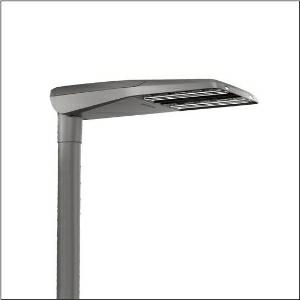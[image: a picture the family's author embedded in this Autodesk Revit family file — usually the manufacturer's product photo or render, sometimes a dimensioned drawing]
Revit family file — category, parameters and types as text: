
# Revit family: streetlight_sl_11_iq_midi___st1_2a_5xc3a51e08le_ac55
name_source: partatom
category: Lighting Fixtures
units: mm (PartAtom-declared; Revit-internal decimal feet)

## family parameters
Cut with Voids When Loaded = No
Host = Face
Light Source = No
Part Type = Normal
Room Calculation Point = No
Round Connector Dimension = Use Diameter
Shared = No

## types (1)
- --- (1 x LED, 9210 lm, 60.4 W, 3000K)
    Apparent Load = 60 VA
    CIE Flux Codes = 32 70 96 100 100
    Color Rendering = 70
    Color Temperature = 3000K
    Default Elevation = 1800 mm
    Description = Streetlight SL 11 iQ midi, mast luminaire, primary light control with 3 zone facetted reflector, of plastic, silver coated, highly specular, primary optical cover: cover, of PMMA, transparent, light distribution: ST1.2a, light emission: direct distribution, primary light characteristic: asymmetric, installation type: post-top, side-entry, lamps: LED, High Power LED, rated values: 9.210lm | 60,4W | 152,5lm/W (begin service life); end service life: 9.210lm | 62,5W; at 50% lumin. flux: 4.605lm | 29,6W | 155,6lm/W, colour temperature: 3000K, colour rendering: CRI > 70, light colour: 730, light setting 1 begin service life: 100% | 9.210lm | 60,4W | 152,5lm/W | 3.000K, light setting 1 end service life: 62,5W, further light settings possible, control: optimised constant luminous flux control (CLO 2.0), Desk-Remote (wireless, voltage-free reading and setting of iQ features in the workshop via application-optimized NFC function/RFID function), Light-Fading, Smart-Wire, Night-Set, Lumen-Switch, Temp-Guard, Auto-Match, with cable H07RN-F 5x 1.5mm², mains connection: 230..240V, AC, 50/60Hz, connection cable pre-assembled, cable length: 8,5m, luminaire housing, of diecast aluminium, powder-coated, Siteco® metallic grey (DB 702S), please order mast flange separately, inclination adjustable without tools: 0°, 5°, 10°, 15° (post-top) | 0°, -5°, -10°, -15° (side-entry), sealing non-destructively replaceable, multi-level sealing system, length: 780mm, width: 376mm, height: 118mm, mast flange for spigot size: 42mm (side-entry): 5XC10008XM4, 60/48mm (side-entry/post-top): 5XC10108XM2, 76/60mm (side-entry/post-top): 5XC10108XM1, equipment: standard, protection rating (complete): IP66, insulation class (complete): insulation class II (safety insulation), certification: CE, ENEC, ENEC+, VDE, impact resistance: IK10, permissible operating ambient temperature for outdoor applications: -25..+50°C, standard-compliant lighting for roads and squares, Environmental Product Declaration (EPD) tested and certified by an independent institute, packaging unit: 1 piece

Light Distribution: ST1.2a
    Height = 118 mm
    Lamp = 1 x LED
    Lamp Light Flux = 9210 lm
    Lamp Power = 60.4 W
    Lamp count = 1
    Length = 780 mm
    Luminous efficacy = 152 lm/W
    Manufacturer = Siteco
    ModVariant = No
    Model = 5XC3A51E08LE
    Number of Poles = 1
    OnlyDefault = Yes
    Power Factor = 1
    Product Name = Streetlight SL 11 iQ midi | ST1.2a
    Product group = mast luminaire | pylon top
    ProductGroupID = 6100
    Protection Class = Protection class II
    Protection Degree = IP 66
    RLX_Detail_Level = 1
    RLX_Emergency_Light_Flux = 0 lm
    RLX_Emergency_Type = 0
    RLX_Emergency_Type_DB = No
    RlxData = <blob elided: 70713 chars, md5=c5067b52>
    Socket = socket
    Standby Power = 0 W
    System Light Flux = 9210 lm
    System Power = 60 W
    Type Comments = factory setting: luminous flux: 100 % | dim-lin: 254 | 520 mA
    Type Image = l_1005960.jpg
    URL = http://relux.com
    VarID = @adj_218279
    Voltage = 0 V
    Weight = 0.00 kg
    Width = 376 mm

## geometry (parser evidence)
native form markers: Blend x4, Sweep x10
no freeform markers — native parametric forms only
